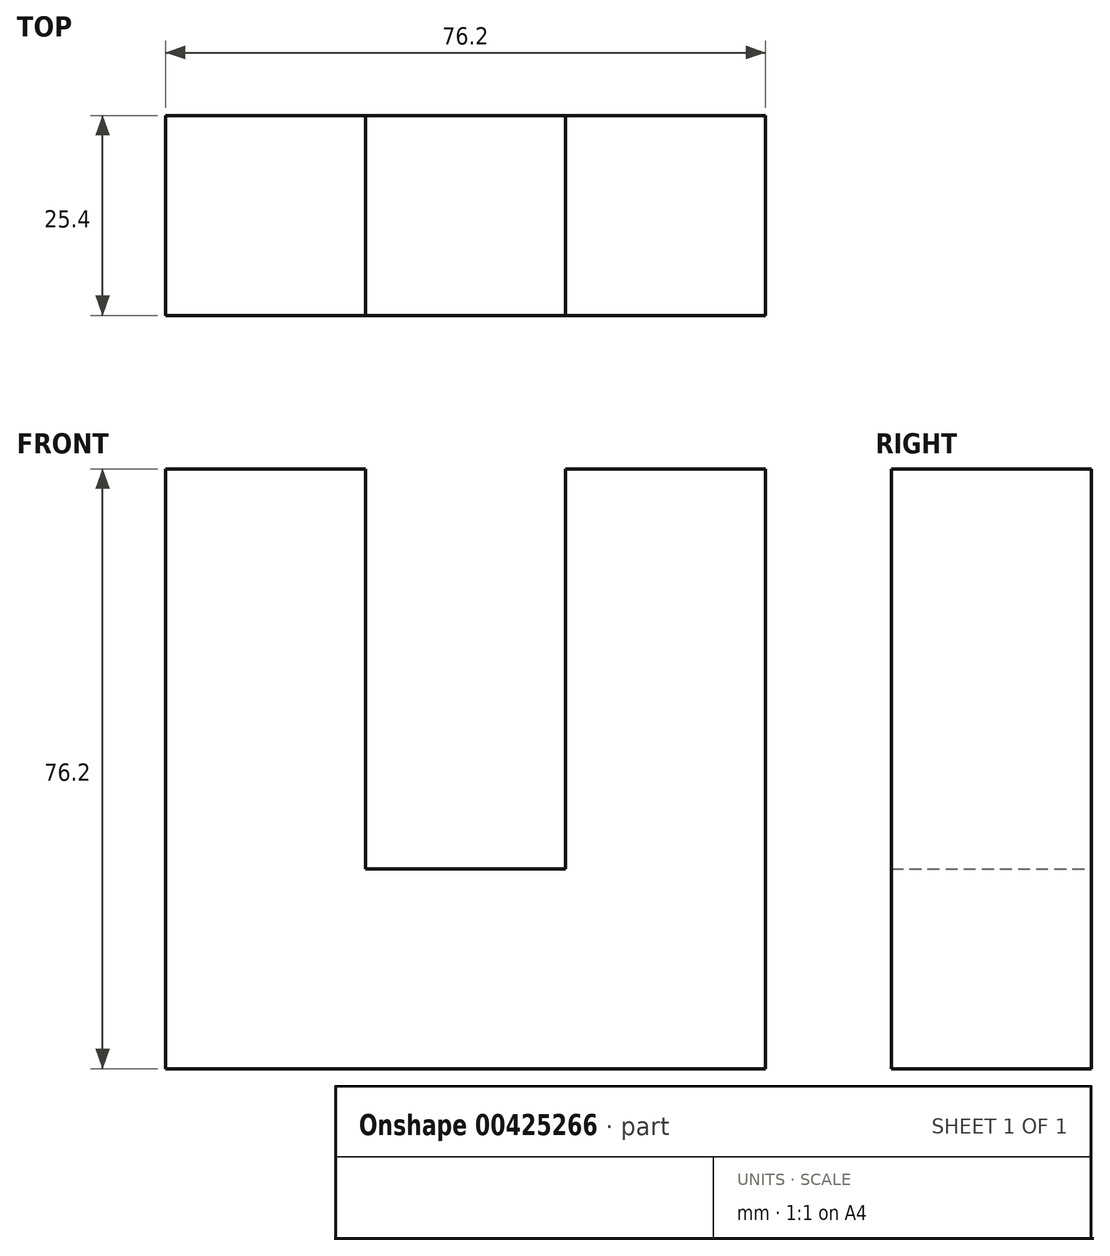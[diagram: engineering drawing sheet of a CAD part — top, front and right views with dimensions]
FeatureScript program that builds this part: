
annotation { "Feature Type Name" : "Feature", "Feature Type Description" : "" }
export const myFeature = defineFeature(function(context is Context, id is Id, definition is map)
    precondition{}
    {
        {
            var Q0;
            Q0=qCreatedBy(makeId("Front.planeOp"),FACE);
            var sketch = newSketch(context, id + "F0", { "sketchPlane" : qUnion([Q0])});
            skLineSegment(sketch, "E0", {"start": v(-37.24, 34.18) * mm, "end": v(-37.24, -42.01) * mm});
            skLineSegment(sketch, "E1", {"start": v(-37.24, -42.01) * mm, "end": v(38.96, -42.01) * mm});
            skLineSegment(sketch, "E2", {"start": v(38.96, -42.01) * mm, "end": v(38.96, 34.19) * mm});
            skLineSegment(sketch, "E3", {"start": v(-37.24, 34.18) * mm, "end": v(-11.84, 34.18) * mm});
            skLineSegment(sketch, "E4", {"start": v(-11.84, 34.18) * mm, "end": v(-11.84, -16.61) * mm});
            skLineSegment(sketch, "E5", {"start": v(-11.84, -16.61) * mm, "end": v(13.56, -16.61) * mm});
            skLineSegment(sketch, "E6", {"start": v(13.56, -16.61) * mm, "end": v(13.56, 34.18) * mm});
            skLineSegment(sketch, "E7", {"start": v(13.56, 34.18) * mm, "end": v(38.96, 34.19) * mm});
            skSolve(sketch);
        }
        {
            var Q0;
            Q0=makeQuery(id+"F0.imprint","IMPRINT",FACE,{"disambiguationData":[TD([[makeQuery(id+"F0.imprint","IMPRINT",EDGE,{"derivedFrom":sQuery(id+"F0.wireOp",EDGE,"E0")}),1.0]])]});
            extrude(context, id + "F1", {"entities" : qUnion([Q0]), "depth" : 25.4 * mm});
        }
    });
